# Revit family: Grinder_Pump-Solid_Handling-Zoeller-71_Horizontal_Series
name_source: partatom
category: Mechanical Equipment
units: mm (PartAtom-declared; Revit-internal decimal feet)

## family parameters
Always vertical = No
Cut with Voids When Loaded = No
OmniClass Number = 23.60.30.21
OmniClass Title = Pumps
Part Type = Normal
Room Calculation Point = No
Round Connector Dimension = Use Radius
Shared = Yes
Work Plane-Based = Yes

## types (3) — shared parameters
Assembly Code = D2010900
Default Elevation = 0"
Description = Commercial Grinder Pumps
Discharge Radius = 1 1/4"
Finish = Cast Iron-Zoeller-Powder Coated Epoxy
Flange = ANSI B16.1
Height = 28 1/4"
Hertz = 60
Impeller Type = Bronze Vortex
Installation Type = Floor Mounted
Insulation = Class F
Lead Wires Insulation = Class F
Length = 13 13/16"
Manufacturer = Zoeller
Material = Cast Iron-Zoeller-Powder Coated Epoxy
Max. Stator Temp. = 311 °F
Max. Water Temp. = 104 °F
Model = 7110-2 1/2"-3"
Moisture Detection = Moisture Sensing Probes (Requires a circuit in control panel to function)
Motor Shaft = 416 S.S.
Motor Thermal Shutoff = Thermal Sensors with Automatic Reset (Requires a circuit in control panel to function)
Motor Type = Submersible
Operation = Non-Automatic
Power Cord = #12-4 SO (Models with a FLA greater than 20 amps use #8-4 gauge power cord)
Price = Prices may vary. Please consult Manufacturer Representative for most up-to-date price list.
Product Documentation Link = https://www.zoellerengineered.com
Product Page URL = https://www.zoellerengineered.com
RPM = 3450
Revised Date = 04/24/2024
Service Factor = 1.2
Shaft Seal Lower (Options) = Carbon/Silicon Carbide, Silicon Carbide/Silicon Carbide
Shaft Seal Lower Standard = Carbon/Ceramic
Shaft Seal Upper (Options) = Carbon/Silicon Carbide Silicon Carbide/Silicon Carbide
Shaft Seal Upper Standard = Carbon/Ceramic
Shipping Weight = 245 lbs (111 kg)
Tandem Seals = Standard
Type SOW Power Cord Length = 300"
URL = https://www.zoellerengineered.com
Voltage = 200V / 230V / 460V
Warranty Information = 36 Months (Limited)
Waste Connection = Yes
Width = 11 3/4"

## per-type parameters (varying)
| type | 3" Discharge Size (Optional) | Discharge Diameter | Full Load Amps (Voltage Dependent) | Locked Rotor Amps (Voltage Dependant) | Maximum KW Input | Motor | Motor Design Letter | NEC Locked Rotor Code | Phase | Type |
| 7110-2.5"-3" | Yes | 2.5 | 6.0-23.6 | 25.2-132.0 | 5.3 | 3.0 BHP | NEMA B (3 Ph), NEMA L (1 Ph) | M (1 Ph), G (3 Ph) | 1 or 3 | Permanent Split Capacitor or 3 Phase |
| 7111-2.5"-3" | No | 2 1/2" | 7.2-28.0 | 36.0-132.0 | 6.4 | 5.0 BHP | NEMA B (3 Ph), NEMA L (1 Ph) | G (1 Ph), H (3 Ph) | 1 or 3 | Permanent Split Capacitor or 3 Phase |
| 7112-2.5"-3" | No | 2 1/2" | 9.0-25.3 | 36.0-94.0 | 8.0 | 7.5 BHP | NEMA B (3 Ph) | D | 3 | Phase |

## geometry (parser evidence)
native form markers: Sweep x2
no freeform markers — native parametric forms only
